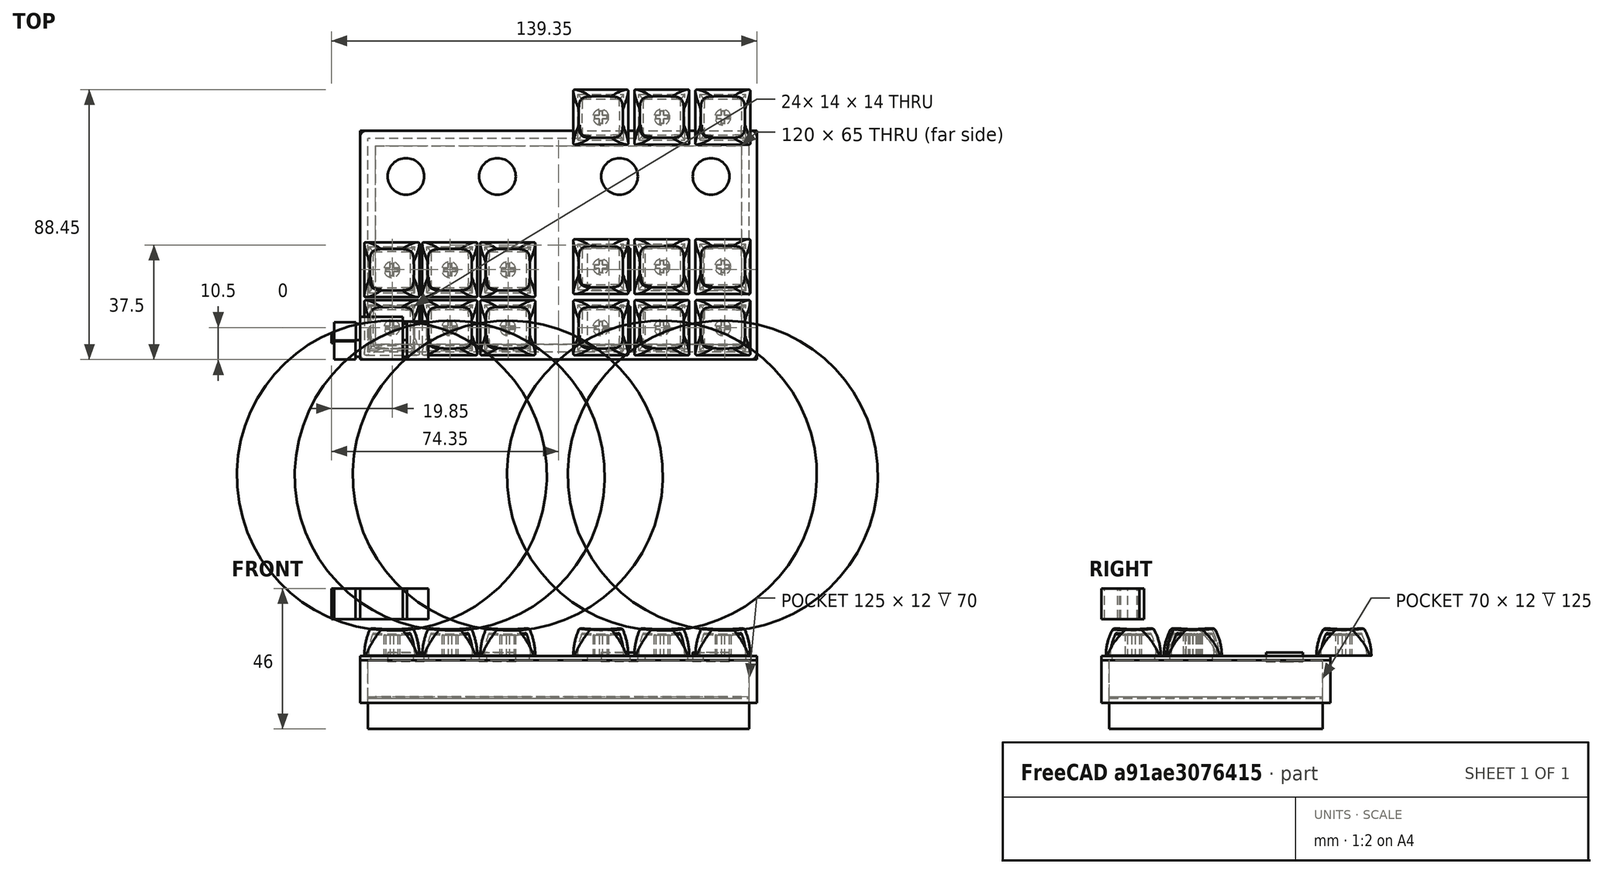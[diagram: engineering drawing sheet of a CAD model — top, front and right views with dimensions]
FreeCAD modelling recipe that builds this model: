
FCSTD DOCUMENT  (FreeCAD 1.0R39109 (Git))
Label: control-v0.6
License: All rights reserved
LicenseURL: https://en.wikipedia.org/wiki/All_rights_reserved
objects: Part::Box×28, Part::Feature×15, Part::Cut×15, Part::Cylinder×4, App::DocumentObjectGroup×4, Part::FeaturePython×1, Part::Fillet×1
note: 64 computed .brp shape members not serialized (recipe doc carries the construction recipe); baked Part::Feature solids carry a one-line shape summary decoded from their .brp

FEATURE [Part::Box] Box  label="Upper Housing"
  AttacherType = Attacher::AttachEngine3D
  Height = 1.35
  Length = 130
  Placement = pos=(0,0,11.5) rot=(0,0,1;0rad)
  Width = 75
FEATURE [Part::Box] Box001  label="Cube"
  AttacherType = Attacher::AttachEngine3D
  Height = 4
  Length = 14
  Placement = pos=(3.5,3.5,10) rot=(0,0,1;0rad)
  Width = 14
FEATURE [Part::Box] Box002  label="Cube001"
  AttacherType = Attacher::AttachEngine3D
  Height = 4
  Length = 14
  Placement = pos=(3.5,22.5,10) rot=(0,0,1;0rad)
  Width = 14
FEATURE [Part::Box] Box003  label="Cube002"
  AttacherType = Attacher::AttachEngine3D
  Height = 4
  Length = 14
  Placement = pos=(22.5,22.5,10) rot=(0,0,1;0rad)
  Width = 14
FEATURE [Part::Box] Box005  label="Cube004"
  AttacherType = Attacher::AttachEngine3D
  Height = 4
  Length = 14
  Placement = pos=(41.5,3.5,10) rot=(0,0,1;0rad)
  Width = 14
FEATURE [Part::Box] Box006  label="Cube005"
  AttacherType = Attacher::AttachEngine3D
  Height = 4
  Length = 14
  Placement = pos=(41.5,22.5,10) rot=(0,0,1;0rad)
  Width = 14
FEATURE [Part::Box] Box007  label="Cube006"
  AttacherType = Attacher::AttachEngine3D
  Height = 4
  Length = 14
  Placement = pos=(112.5,3.5,10) rot=(0,0,1;0rad)
  Width = 14
FEATURE [Part::Box] Box008  label="Cube007"
  AttacherType = Attacher::AttachEngine3D
  Height = 4
  Length = 14
  Placement = pos=(93.5,3.5,10) rot=(0,0,1;0rad)
  Width = 14
FEATURE [Part::Box] Box009  label="Cube008"
  AttacherType = Attacher::AttachEngine3D
  Height = 4
  Length = 14
  Placement = pos=(74.5,3.5,10) rot=(0,0,1;0rad)
  Width = 14
FEATURE [Part::Box] Box010  label="Cube009"
  AttacherType = Attacher::AttachEngine3D
  Height = 4
  Length = 14
  Placement = pos=(74.5,22.5,10) rot=(0,0,1;0rad)
  Width = 14
FEATURE [Part::Box] Box011  label="Cube010"
  AttacherType = Attacher::AttachEngine3D
  Height = 4
  Length = 14
  Placement = pos=(93.5,22.5,10) rot=(0,0,1;0rad)
  Width = 14
FEATURE [Part::Box] Box012  label="Cube011"
  AttacherType = Attacher::AttachEngine3D
  Height = 4
  Length = 14
  Placement = pos=(112.5,22.5,10) rot=(0,0,1;0rad)
  Width = 14
FEATURE [Part::Cylinder] Cylinder
  Angle = 360
  AttacherType = Attacher::AttachEngine3D
  FirstAngle = 0
  Height = 3
  Placement = pos=(15,60,11) rot=(0,0,1;0rad)
  Radius = 6
  SecondAngle = 0
FEATURE [Part::Cylinder] Cylinder001
  Angle = 360
  AttacherType = Attacher::AttachEngine3D
  FirstAngle = 0
  Height = 3
  Placement = pos=(45,60,11) rot=(0,0,1;0rad)
  Radius = 6
  SecondAngle = 0
FEATURE [Part::Feature] Part__Feature  label="1u v2"
  Placement = pos=(21.5,15,13) rot=(1,0,0;1.5708rad)
  shape: bbox 18 x 18.01 x 11.79 mm, 51 faces (baked)
FEATURE [Part::Box] Box004  label="Cube003"
  AttacherType = Attacher::AttachEngine3D
  Height = 4
  Length = 14
  Placement = pos=(22.5,3.5,10) rot=(0,0,1;0rad)
  Width = 14
FEATURE [Part::Feature] Part__Feature001  label="1u v003"
  Placement = pos=(40.5,15,13) rot=(1,0,0;1.5708rad)
  shape: bbox 18 x 18.01 x 11.79 mm, 51 faces (baked)
FEATURE [Part::Feature] Part__Feature002  label="1u v004"
  Placement = pos=(59.5,15,13) rot=(1,0,0;1.5708rad)
  shape: bbox 18 x 18.01 x 11.79 mm, 51 faces (baked)
FEATURE [Part::Feature] Part__Feature003  label="1u v005"
  Placement = pos=(59.5,34,13) rot=(1,0,0;1.5708rad)
  shape: bbox 18 x 18.01 x 11.79 mm, 51 faces (baked)
FEATURE [Part::Feature] Part__Feature004  label="1u v006"
  Placement = pos=(21.5,34,13) rot=(1,0,0;1.5708rad)
  shape: bbox 18 x 18.01 x 11.79 mm, 51 faces (baked)
FEATURE [Part::Feature] Part__Feature005  label="1u v007"
  Placement = pos=(40.5,34,13) rot=(1,0,0;1.5708rad)
  shape: bbox 18 x 18.01 x 11.79 mm, 51 faces (baked)
FEATURE [Part::Feature] Part__Feature006  label="1u v008"
  Placement = pos=(90,35,13) rot=(1,0,0;1.5708rad)
  shape: bbox 18 x 18.01 x 11.79 mm, 51 faces (baked)
FEATURE [Part::Feature] Part__Feature007  label="1u v009"
  Placement = pos=(90,15,13) rot=(1,0,0;1.5708rad)
  shape: bbox 18 x 18.01 x 11.79 mm, 51 faces (baked)
FEATURE [Part::Feature] Part__Feature008  label="1u v010"
  Placement = pos=(110,15,13) rot=(1,0,0;1.5708rad)
  shape: bbox 18 x 18.01 x 11.79 mm, 51 faces (baked)
FEATURE [Part::Feature] Part__Feature009  label="1u v011"
  Placement = pos=(110,35,13) rot=(1,0,0;1.5708rad)
  shape: bbox 18 x 18.01 x 11.79 mm, 51 faces (baked)
FEATURE [Part::Feature] Part__Feature010  label="1u v012"
  Placement = pos=(130,15,13) rot=(1,0,0;1.5708rad)
  shape: bbox 18 x 18.01 x 11.79 mm, 51 faces (baked)
FEATURE [Part::Feature] Part__Feature011  label="1u v013"
  Placement = pos=(130,35,13) rot=(1,0,0;1.5708rad)
  shape: bbox 18 x 18.01 x 11.79 mm, 51 faces (baked)
FEATURE [Part::Feature] Part__Feature012  label="1u v014"
  Placement = pos=(130,84,13) rot=(1,0,0;1.5708rad)
  shape: bbox 18 x 18.01 x 11.79 mm, 51 faces (baked)
FEATURE [Part::Feature] Part__Feature013  label="1u v015"
  Placement = pos=(110,84,13) rot=(1,0,0;1.5708rad)
  shape: bbox 18 x 18.01 x 11.79 mm, 51 faces (baked)
FEATURE [Part::Feature] Part__Feature014  label="1u v016"
  Placement = pos=(90,84,13) rot=(1,0,0;1.5708rad)
  shape: bbox 18 x 18.01 x 11.79 mm, 51 faces (baked)
FEATURE [App::DocumentObjectGroup] Group004  label="Keycaps"
  Group = -> [Part__Feature,Part__Feature001,Part__Feature002,Part__Feature004,Part__Feature005,Part__Feature003,Part__Feature007,Part__Feature008,Part__Feature010,Part__Feature006,Part__Feature009,Part__Feature011,Part__Feature012,Part__Feature013,Part__Feature014]
FEATURE [Part::Cut] Cut
  Base = -> Box
  Tool = -> Box001
FEATURE [Part::Cut] Cut001
  Base = -> Cut
  Tool = -> Box004
FEATURE [Part::Cut] Cut002
  Base = -> Cut001
  Tool = -> Box005
FEATURE [Part::Cut] Cut003
  Base = -> Cut002
  Tool = -> Box002
FEATURE [Part::Cut] Cut004
  Base = -> Cut003
  Tool = -> Box003
FEATURE [Part::Cut] Cut005
  Base = -> Cut004
  Tool = -> Box006
FEATURE [Part::Cut] Cut006
  Base = -> Cut005
  Tool = -> Box009
FEATURE [Part::Cut] Cut007
  Base = -> Cut006
  Tool = -> Box008
FEATURE [Part::Cut] Cut008
  Base = -> Cut007
  Tool = -> Box007
FEATURE [Part::Cut] Cut009
  Base = -> Cut008
  Tool = -> Box010
FEATURE [Part::Cut] Cut010
  Base = -> Cut009
  Tool = -> Box011
FEATURE [Part::Cut] Cut011
  Base = -> Cut010
  Tool = -> Box012
FEATURE [App::DocumentObjectGroup] Group001  label="Upper Housing2"
  Group = -> [Cut011]
FEATURE [Part::Box] Box016  label="Cube015"
  AttacherType = Attacher::AttachEngine3D
  Height = 15
  Length = 130
  Placement = pos=(0,0,-13.5) rot=(0,0,1;0rad)
  Width = 75
FEATURE [Part::Box] Box017  label="Cube016"
  AttacherType = Attacher::AttachEngine3D
  Height = 17.5
  Length = 125
  Placement = pos=(2.5,2.5,-11.5) rot=(0,0,1;0rad)
  Width = 70
FEATURE [Part::Box] Box018  label="Cube017"
  AttacherType = Attacher::AttachEngine3D
  Height = 10
  Length = 125
  Placement = pos=(2.5,2.5,-11) rot=(0,0,1;0rad)
  Width = 70
FEATURE [Part::Cut] Cut012
  Base = -> Box016
  Placement = pos=(0,0,11) rot=(0,0,1;0rad)
  Tool = -> Box017
FEATURE [Part::Box] Box019  label="Cube018"
  AttacherType = Attacher::AttachEngine3D
  Height = 10
  Length = 14
  Placement = pos=(0,0,25) rot=(0,0,1;0rad)
  Width = 14
FEATURE [Part::Box] Box020  label="Cube019"
  AttacherType = Attacher::AttachEngine3D
  Height = 10
  Length = 1.35
  Placement = pos=(14,6.35,25) rot=(0,0,1;0rad)
  Width = 5.35
FEATURE [Part::Box] Box021  label="Cube020"
  AttacherType = Attacher::AttachEngine3D
  Height = 10
  Length = 1.4
  Placement = pos=(14,1,25) rot=(0,0,1;0rad)
  Width = 5.35
FEATURE [Part::Box] Box022  label="Cube021"
  AttacherType = Attacher::AttachEngine3D
  Height = 10
  Length = 1.45
  Placement = pos=(-1.45,6.35,25) rot=(0,0,1;0rad)
  Width = 5.35
FEATURE [Part::Box] Box023  label="Cube022"
  AttacherType = Attacher::AttachEngine3D
  Height = 10
  Length = 1.5
  Placement = pos=(-1.5,1,25) rot=(0,0,1;0rad)
  Width = 5.35
FEATURE [Part::Box] Box024  label="Cube023"
  AttacherType = Attacher::AttachEngine3D
  Height = 10
  Length = 7
  Placement = pos=(-8.45,6,25) rot=(0,0,1;0rad)
  Width = 6.22
FEATURE [Part::Box] Box025  label="Cube024"
  AttacherType = Attacher::AttachEngine3D
  Height = 10
  Length = 0.9
  Placement = pos=(-9.35,5.35,25) rot=(0,0,1;0rad)
  Width = 3.3
FEATURE [Part::Box] Box026  label="Cube025"
  AttacherType = Attacher::AttachEngine3D
  Height = 10
  Length = 7
  Placement = pos=(15.4,0,25) rot=(0,0,1;0rad)
  Width = 12.45
FEATURE [Part::Box] Box027  label="Cube026"
  AttacherType = Attacher::AttachEngine3D
  Height = 10
  Length = 7
  Placement = pos=(-8.5,0,25) rot=(0,0,1;0rad)
  Width = 6.22
FEATURE [App::DocumentObjectGroup] Group  label="Stab"
  Group = -> [Box019,Box022,Box021,Box023,Box024,Box027,Box025,Box026,Box020]
FEATURE [Part::Box] Box028  label="Cube027"
  AttacherType = Attacher::AttachEngine3D
  Height = 10
  Length = 125
  Placement = pos=(2.5,2.5,-11) rot=(0,0,1;0rad)
  Width = 70
FEATURE [Part::Box] Box029  label="Cube028"
  AttacherType = Attacher::AttachEngine3D
  Height = 14
  Length = 120
  Placement = pos=(5,5,-2.5) rot=(0,0,1;0rad)
  Width = 65
FEATURE [Part::Cut] Cut013
  Base = -> Cut012
  Tool = -> Box029
FEATURE [Part::Box] Box030  label="Lower Housing"
  AttacherType = Attacher::AttachEngine3D
  Height = 2
  Length = 125
  Placement = pos=(2.5,2.5,-2.5) rot=(0,0,1;0rad)
  Width = 70
FEATURE [Part::Cut] Cut014
  Base = -> Cut013
  Tool = -> Box028
FEATURE [Part::FeaturePython] Connect  label="Upper Housing003"  # WARN: FeaturePython — macro-defined, semantics opaque (R4)
  Objects = -> [Group001,Cut014]
  Tolerance = 0
FEATURE [Part::Fillet] Fillet
  Base = -> Connect
  EdgeLinks = -> Connect [Edge5,Edge7,Edge13,Edge14,Edge50,Edge52,Edge102,Edge104,Edge141,Edge150,Edge203,Edge204]
  Edges = 12 edges r=2: [Edge5,Edge7,Edge13,Edge14,Edge50,Edge52,Edge102,Edge104,Edge141,Edge150,Edge203,Edge204]
FEATURE [Part::Cylinder] Cylinder003
  Angle = 360
  AttacherType = Attacher::AttachEngine3D
  FirstAngle = 0
  Height = 3
  Placement = pos=(85,60,11) rot=(0,0,1;0rad)
  Radius = 6
  SecondAngle = 0
FEATURE [Part::Cylinder] Cylinder002
  Angle = 360
  AttacherType = Attacher::AttachEngine3D
  FirstAngle = 0
  Height = 3
  Placement = pos=(115,60,11) rot=(0,0,1;0rad)
  Radius = 6
  SecondAngle = 0
FEATURE [App::DocumentObjectGroup] Group003  label="Rotories"
  Group = -> [Cylinder,Cylinder001,Cylinder003,Cylinder002]
